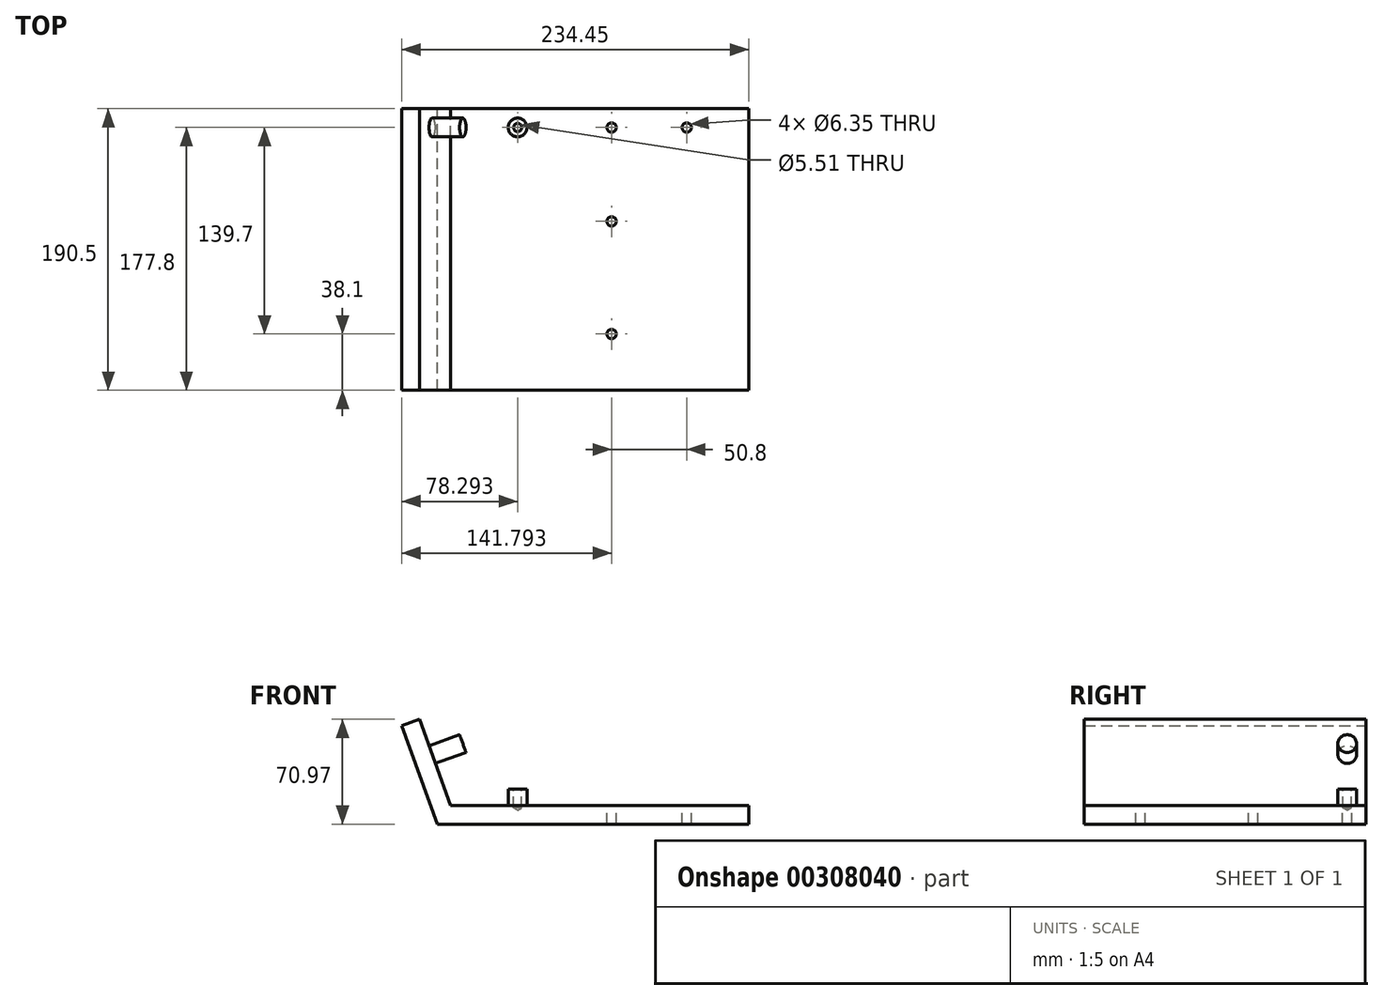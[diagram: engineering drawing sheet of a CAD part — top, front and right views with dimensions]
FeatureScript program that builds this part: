
annotation { "Feature Type Name" : "Feature", "Feature Type Description" : "" }
export const myFeature = defineFeature(function(context is Context, id is Id, definition is map)
    precondition{}
    {
        {
            var Q0;
            Q0=qCreatedBy(makeId("Front.planeOp"),FACE);
            var sketch = newSketch(context, id + "F0", { "sketchPlane" : qUnion([Q0])});
            skLineSegment(sketch, "E0", {"start": v(-111.04, -3.38) * mm, "end": v(99.5, -3.38) * mm});
            skLineSegment(sketch, "E1", {"start": v(99.5, -3.38) * mm, "end": v(99.5, 9.32) * mm});
            skPoint(sketch, "E2.end.orphan", {"position": v(-111.04, 9.32) * mm});
            skLineSegment(sketch, "E3", {"start": v(-111.04, -3.38) * mm, "end": v(-134.95, 63.3) * mm});
            skPoint(sketch, "E4.start.orphan", {"position": v(-139.39, -3.38) * mm});
            skLineSegment(sketch, "E5", {"start": v(-134.95, 63.3) * mm, "end": v(-123, 67.59) * mm});
            skPoint(sketch, "E5.endSnap0", {"position": v(-123, 29.96) * mm});
            skLineSegment(sketch, "E6", {"start": v(-123, 67.59) * mm, "end": v(-102.1, 9.32) * mm});
            skLineSegment(sketch, "E7", {"start": v(99.5, 9.32) * mm, "end": v(-102.1, 9.32) * mm});
            skLineSegment(sketch, "E8", {"start": v(19.64, 118.2) * mm, "end": v(61.42, 139.9) * mm});
            skSolve(sketch);
        }
        {
            var Q0;
            Q0=makeQuery(id+"F0.imprint","IMPRINT",FACE,{"disambiguationData":[TD([[makeQuery(id+"F0.imprint","IMPRINT",EDGE,{"derivedFrom":sQuery(id+"F0.wireOp",EDGE,"E0")}),1.0]])]});
            extrude(context, id + "F1", {"entities" : qUnion([Q0]), "depth" : 190.5 * mm});
        }
        {
            var Q0;
            Q0=makeQuery(id+"F1.opExtrude","SWEPT_FACE",FACE,{"disambiguationData":[OSD([sQuery(id+"F0.wireOp",EDGE,"E7")])]});
            var sketch = newSketch(context, id + "F2", { "sketchPlane" : qUnion([Q0])});
            skCircle(sketch, "E9", {"center": v(6.84, -152.4) * mm, "radius": 3.18 * mm});
            skCircle(sketch, "E10", {"center": v(6.84, -76.2) * mm, "radius": 3.18 * mm});
            skCircle(sketch, "E11", {"center": v(6.84, -12.7) * mm, "radius": 3.18 * mm});
            skCircle(sketch, "E12", {"center": v(57.64, -12.7) * mm, "radius": 3.18 * mm});
            skSolve(sketch);
        }
        {
            var Q0;
            Q0 = qSketchRegion(id + "F2", true);
            extrude(context, id + "F3", {"entities" : qUnion([Q0]), "operationType" : NewBodyOperationType.REMOVE, "endBound" : BoundingType.THROUGH_ALL, "oppositeDirection" : true, "depth" : 25.4 * mm});
        }
        {
            var Q0;
            Q0=makeQuery(id+"F1.opExtrude","SWEPT_FACE",FACE,{"disambiguationData":[OSD([sQuery(id+"F0.wireOp",EDGE,"E7")])]});
            var sketch = newSketch(context, id + "F4", { "sketchPlane" : qUnion([Q0])});
            skCircle(sketch, "E13", {"center": v(-56.66, -12.7) * mm, "radius": 6.35 * mm});
            skSolve(sketch);
        }
        {
            var Q0;
            Q0 = qSketchRegion(id + "F4", true);
            extrude(context, id + "F5", {"entities" : qUnion([Q0]), "operationType" : NewBodyOperationType.ADD, "depth" : 11 * mm});
        }
        {
            var Q0;
            Q0=makeQuery(id+"F1.opExtrude","SWEPT_FACE",FACE,{"disambiguationData":[OSD([sQuery(id+"F0.wireOp",EDGE,"E6")])]});
            var sketch = newSketch(context, id + "F6", { "sketchPlane" : qUnion([Q0])});
            skCircle(sketch, "E14", {"center": v(-12.7, 79.73) * mm, "radius": 6.35 * mm});
            skSolve(sketch);
        }
        {
            var Q0;
            Q0 = qSketchRegion(id + "F6", true);
            extrude(context, id + "F7", {"entities" : qUnion([Q0]), "operationType" : NewBodyOperationType.ADD, "depth" : 22 * mm});
        }
        {
            var Q0;
            Q0=makeQuery(id+"F5.opExtrude","CAP_FACE",FACE,{"disambiguationData":[OSD([sQuery(id+"F4.wireOp",EDGE,"E13")])],"isStart":false});
            var sketch = newSketch(context, id + "F8", { "sketchPlane" : qUnion([Q0])});
            skPoint(sketch, "E15", {"position": v(-56.66, -12.7) * mm});
            skSolve(sketch);
        }
        {
            var Q0;
            Q0=sQuery(id+"F8.wireOp",VERTEX,"E15");
            var Q1;
            Q1=makeQuery(id+"F1.opExtrude","SWEPT_BODY",BODY,{"disambiguationData":[OSD([sQuery(id+"F0.wireOp",EDGE,"E0"),sQuery(id+"F0.wireOp",EDGE,"E1"),sQuery(id+"F0.wireOp",EDGE,"E3"),sQuery(id+"F0.wireOp",EDGE,"E5"),sQuery(id+"F0.wireOp",EDGE,"E6"),sQuery(id+"F0.wireOp",EDGE,"E7")])]});
            hole(context, id + "F9", {"style" : HoleStyle.SIMPLE, "endStyle" : HoleEndStyle.BLIND, "holeDiameter" : 5.5 * mm, "holeDepth" : 12.7 * mm, "tappedDepth" : 12.7 * mm, "tapClearance" : 3, "locations" : qUnion([Q0]), "scope" : qUnion([Q1])});
        }
    });
